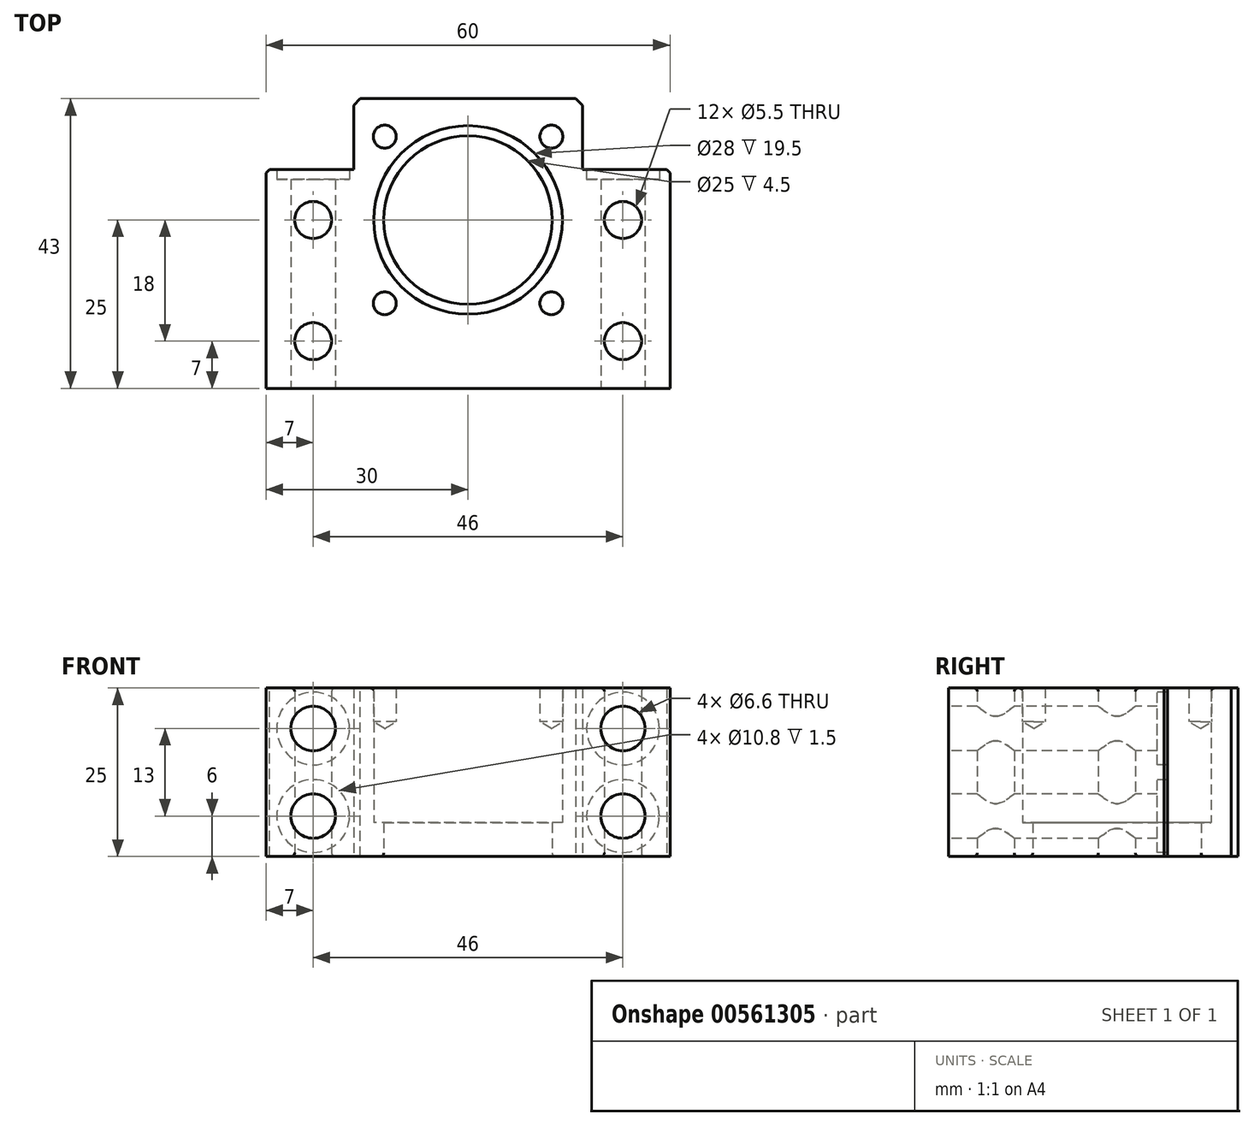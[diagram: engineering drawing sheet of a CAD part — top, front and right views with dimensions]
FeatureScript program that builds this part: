
annotation { "Feature Type Name" : "Feature", "Feature Type Description" : "" }
export const myFeature = defineFeature(function(context is Context, id is Id, definition is map)
    precondition{}
    {
        {
            var Q0;
            Q0=qCreatedBy(makeId("Top.planeOp"),FACE);
            var sketch = newSketch(context, id + "F0", { "sketchPlane" : qUnion([Q0])});
            skLineSegment(sketch, "E0", {"start": v(-30, -25) * mm, "end": v(30, -25) * mm});
            skLineSegment(sketch, "E1", {"start": v(30, -25) * mm, "end": v(30, 7.5) * mm});
            skLineSegment(sketch, "E2", {"start": v(30, 7.5) * mm, "end": v(17, 7.5) * mm});
            skLineSegment(sketch, "E3", {"start": v(17, 7.5) * mm, "end": v(17, 18) * mm});
            skLineSegment(sketch, "E4", {"start": v(17, 18) * mm, "end": v(-17, 18) * mm});
            skLineSegment(sketch, "E5", {"start": v(-17, 18) * mm, "end": v(-17, 7.5) * mm});
            skLineSegment(sketch, "E6", {"start": v(-17, 7.5) * mm, "end": v(-30, 7.5) * mm});
            skLineSegment(sketch, "E7", {"start": v(-30, 7.5) * mm, "end": v(-30, -25) * mm});
            skCircle(sketch, "E8", {"center": v(0, 0) * mm, "radius": 14 * mm});
            skPoint(sketch, "E9", {"position": v(-23, 0) * mm});
            skPoint(sketch, "E10", {"position": v(-23, -18) * mm});
            skCircle(sketch, "E11", {"center": v(-23, 0) * mm, "radius": 2.75 * mm});
            skCircle(sketch, "E12", {"center": v(-23, -18) * mm, "radius": 2.75 * mm});
            skCircle(sketch, "E13.MirrorC", {"center": v(23, 0) * mm, "radius": 2.75 * mm});
            skCircle(sketch, "E14.MirrorC", {"center": v(23, -18) * mm, "radius": 2.75 * mm});
            skSolve(sketch);
        }
        {
            var Q0;
            Q0=makeQuery(id+"F0.imprint","IMPRINT",FACE,{"disambiguationData":[TD([[makeQuery(id+"F0.imprint","IMPRINT",EDGE,{"derivedFrom":sQuery(id+"F0.wireOp",EDGE,"E0")}),1.0]])]});
            extrude(context, id + "F1", {"entities" : qUnion([Q0]), "depth" : 12.5 * mm, "offsetDistance" : 25 * mm, "hasSecondDirection" : true, "secondDirectionOppositeDirection" : true, "secondDirectionDepth" : 12.5 * mm});
        }
        {
            var Q0;
            Q0=makeQuery(id+"F1.opExtrude","SWEPT_EDGE",EDGE,{"disambiguationData":[OSD([sQuery(id+"F0.wireOp",EDGE,"E6"),sQuery(id+"F0.wireOp",EDGE,"E7")])]});
            var Q1;
            Q1=makeQuery(id+"F1.opExtrude","SWEPT_EDGE",EDGE,{"disambiguationData":[OSD([sQuery(id+"F0.wireOp",EDGE,"E1"),sQuery(id+"F0.wireOp",EDGE,"E2")])]});
            chamfer(context, id + "F2", {"entities" : qUnion([Q0, Q1]), "width" : .5 * mm, "tangentPropagation" : true});
        }
        {
            var Q0;
            Q0=makeQuery(id+"F1.opExtrude","SWEPT_EDGE",EDGE,{"disambiguationData":[OSD([sQuery(id+"F0.wireOp",EDGE,"E4"),sQuery(id+"F0.wireOp",EDGE,"E5")])]});
            var Q1;
            Q1=makeQuery(id+"F1.opExtrude","SWEPT_EDGE",EDGE,{"disambiguationData":[OSD([sQuery(id+"F0.wireOp",EDGE,"E3"),sQuery(id+"F0.wireOp",EDGE,"E4")])]});
            chamfer(context, id + "F3", {"entities" : qUnion([Q0, Q1]), "width" : 1 * mm, "tangentPropagation" : true});
        }
        {
            var Q0;
            Q0=makeQuery(id+"F1.opExtrude","SWEPT_FACE",FACE,{"disambiguationData":[OSD([sQuery(id+"F0.wireOp",EDGE,"E11")])]});
            var Q1;
            Q1=makeQuery(id+"F1.opExtrude","SWEPT_FACE",FACE,{"disambiguationData":[OSD([sQuery(id+"F0.wireOp",EDGE,"E12")])]});
            var Q2;
            Q2=makeQuery(id+"F1.opExtrude","SWEPT_FACE",FACE,{"disambiguationData":[OSD([sQuery(id+"F0.wireOp",EDGE,"E13.MirrorC")])]});
            var Q3;
            Q3=makeQuery(id+"F1.opExtrude","SWEPT_FACE",FACE,{"disambiguationData":[OSD([sQuery(id+"F0.wireOp",EDGE,"E14.MirrorC")])]});
            var Q4;
            Q4=makeQuery(id+"F1.opExtrude","CAP_EDGE",EDGE,{"disambiguationData":[OSD([sQuery(id+"F0.wireOp",EDGE,"E8")])],"isStart":false});
            fillet(context, id + "F4", {"entities" : qUnion([Q0, Q1, Q2, Q3, Q4]), "radius" : .5 * mm, "tangentPropagation" : true, "allowEdgeOverflow" : false});
        }
        {
            var Q0;
            Q0=makeQuery(id+"F1.opExtrude","CAP_FACE",FACE,{"disambiguationData":[OSD([sQuery(id+"F0.wireOp",EDGE,"E0"),sQuery(id+"F0.wireOp",EDGE,"E1"),sQuery(id+"F0.wireOp",EDGE,"E2"),sQuery(id+"F0.wireOp",EDGE,"E3"),sQuery(id+"F0.wireOp",EDGE,"E4"),sQuery(id+"F0.wireOp",EDGE,"E5"),sQuery(id+"F0.wireOp",EDGE,"E6"),sQuery(id+"F0.wireOp",EDGE,"E7"),sQuery(id+"F0.wireOp",EDGE,"E8"),sQuery(id+"F0.wireOp",EDGE,"E11"),sQuery(id+"F0.wireOp",EDGE,"E12"),sQuery(id+"F0.wireOp",EDGE,"E13.MirrorC"),sQuery(id+"F0.wireOp",EDGE,"E14.MirrorC")])],"isStart":false});
            var sketch = newSketch(context, id + "F5", { "sketchPlane" : qUnion([Q0])});
            skCircle(sketch, "E15", {"center": v(0, 0) * mm, "radius": 17.5 * mm, "construction": true});
            skLineSegment(sketch, "E16", {"start": v(0, 0) * mm, "end": v(-12.37, 12.37) * mm, "construction": true});
            skPoint(sketch, "E17", {"position": v(-12.37, 12.37) * mm});
            skPoint(sketch, "E18.MirrorP", {"position": v(12.37, 12.37) * mm});
            skPoint(sketch, "E19.MirrorP", {"position": v(12.37, -12.37) * mm});
            skPoint(sketch, "E20.MirrorP", {"position": v(-12.37, -12.37) * mm});
            skSolve(sketch);
        }
        {
            var Q0;
            Q0=sQuery(id+"F5.wireOp",VERTEX,"E17");
            var Q1;
            Q1=sQuery(id+"F5.wireOp",VERTEX,"E18.MirrorP");
            var Q2;
            Q2=sQuery(id+"F5.wireOp",VERTEX,"E19.MirrorP");
            var Q3;
            Q3=sQuery(id+"F5.wireOp",VERTEX,"E20.MirrorP");
            var Q4;
            Q4=makeQuery(id+"F1.opExtrude","SWEPT_BODY",BODY,{"disambiguationData":[OSD([sQuery(id+"F0.wireOp",EDGE,"E0"),sQuery(id+"F0.wireOp",EDGE,"E1"),sQuery(id+"F0.wireOp",EDGE,"E2"),sQuery(id+"F0.wireOp",EDGE,"E3"),sQuery(id+"F0.wireOp",EDGE,"E4"),sQuery(id+"F0.wireOp",EDGE,"E5"),sQuery(id+"F0.wireOp",EDGE,"E6"),sQuery(id+"F0.wireOp",EDGE,"E7"),sQuery(id+"F0.wireOp",EDGE,"E8"),sQuery(id+"F0.wireOp",EDGE,"E11"),sQuery(id+"F0.wireOp",EDGE,"E12"),sQuery(id+"F0.wireOp",EDGE,"E13.MirrorC"),sQuery(id+"F0.wireOp",EDGE,"E14.MirrorC")])]});
            hole(context, id + "F6", {"style" : HoleStyle.SIMPLE, "endStyle" : HoleEndStyle.BLIND, "holeDiameter" : 3.4 * mm, "holeDepth" : 5 * mm, "isTappedThrough" : true, "tappedDepth" : 12 * mm, "tapClearance" : 3, "locations" : qUnion([Q0, Q1, Q2, Q3]), "scope" : qUnion([Q4]), "startStyle" : HoleStartStyle.SKETCH});
        }
        {
            var Q0;
            Q0=makeQuery(id+"F1.opExtrude","CAP_FACE",FACE,{"disambiguationData":[OSD([sQuery(id+"F0.wireOp",EDGE,"E0"),sQuery(id+"F0.wireOp",EDGE,"E1"),sQuery(id+"F0.wireOp",EDGE,"E2"),sQuery(id+"F0.wireOp",EDGE,"E3"),sQuery(id+"F0.wireOp",EDGE,"E4"),sQuery(id+"F0.wireOp",EDGE,"E5"),sQuery(id+"F0.wireOp",EDGE,"E6"),sQuery(id+"F0.wireOp",EDGE,"E7"),sQuery(id+"F0.wireOp",EDGE,"E8"),sQuery(id+"F0.wireOp",EDGE,"E11"),sQuery(id+"F0.wireOp",EDGE,"E12"),sQuery(id+"F0.wireOp",EDGE,"E13.MirrorC"),sQuery(id+"F0.wireOp",EDGE,"E14.MirrorC")])],"isStart":true});
            var sketch = newSketch(context, id + "F7", { "sketchPlane" : qUnion([Q0])});
            skCircle(sketch, "E21", {"center": v(0, 0) * mm, "radius": 12.5 * mm});
            skSolve(sketch);
        }
        {
            var Q0;
            Q0=makeQuery(id+"F7.imprint","IMPRINT",FACE,{"disambiguationData":[TD([[makeQuery(id+"F7.imprint","IMPRINT",EDGE,{"derivedFrom":sQuery(id+"F7.wireOp",EDGE,"E21")}),-1.0]])]});
            extrude(context, id + "F8", {"entities" : qUnion([Q0]), "operationType" : NewBodyOperationType.ADD, "oppositeDirection" : true, "depth" : 5 * mm, "offsetDistance" : 25 * mm});
        }
        {
            var Q0;
            Q0=makeQuery(id+"F8.opExtrude","CAP_EDGE",EDGE,{"disambiguationData":[OSD([sQuery(id+"F7.wireOp",EDGE,"E21")])],"isStart":true});
            fillet(context, id + "F9", {"entities" : qUnion([Q0]), "radius" : .5 * mm, "tangentPropagation" : true, "allowEdgeOverflow" : false});
        }
        {
            var Q0;
            Q0=makeQuery(id+"F1.opExtrude","SWEPT_FACE",FACE,{"disambiguationData":[OSD([sQuery(id+"F0.wireOp",EDGE,"E2")])]});
            var sketch = newSketch(context, id + "F10", { "sketchPlane" : qUnion([Q0])});
            skPoint(sketch, "E22", {"position": v(-23, 6.5) * mm});
            skPoint(sketch, "E23", {"position": v(-23, -6.5) * mm});
            skPoint(sketch, "E24.MirrorP", {"position": v(23, 6.5) * mm});
            skPoint(sketch, "E25.MirrorP", {"position": v(23, -6.5) * mm});
            skSolve(sketch);
        }
        {
            var Q0;
            Q0=sQuery(id+"F10.wireOp",VERTEX,"E22");
            var Q1;
            Q1=sQuery(id+"F10.wireOp",VERTEX,"E23");
            var Q2;
            Q2=sQuery(id+"F10.wireOp",VERTEX,"E24.MirrorP");
            var Q3;
            Q3=sQuery(id+"F10.wireOp",VERTEX,"E25.MirrorP");
            var Q4;
            Q4=makeQuery(id+"F1.opExtrude","SWEPT_BODY",BODY,{"disambiguationData":[OSD([sQuery(id+"F0.wireOp",EDGE,"E0"),sQuery(id+"F0.wireOp",EDGE,"E1"),sQuery(id+"F0.wireOp",EDGE,"E2"),sQuery(id+"F0.wireOp",EDGE,"E3"),sQuery(id+"F0.wireOp",EDGE,"E4"),sQuery(id+"F0.wireOp",EDGE,"E5"),sQuery(id+"F0.wireOp",EDGE,"E6"),sQuery(id+"F0.wireOp",EDGE,"E7"),sQuery(id+"F0.wireOp",EDGE,"E8"),sQuery(id+"F0.wireOp",EDGE,"E11"),sQuery(id+"F0.wireOp",EDGE,"E12"),sQuery(id+"F0.wireOp",EDGE,"E13.MirrorC"),sQuery(id+"F0.wireOp",EDGE,"E14.MirrorC")])]});
            hole(context, id + "F11", {"style" : HoleStyle.C_BORE, "endStyle" : HoleEndStyle.THROUGH, "holeDiameter" : 6.6 * mm, "cBoreDiameter" : 10.8 * mm, "cBoreDepth" : 1.5 * mm, "isTappedThrough" : true, "tappedDepth" : 12 * mm, "tapClearance" : 3, "locations" : qUnion([Q0, Q1, Q2, Q3]), "scope" : qUnion([Q4]), "startStyle" : HoleStartStyle.SKETCH});
        }
    });
